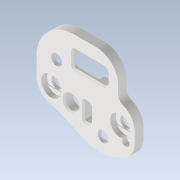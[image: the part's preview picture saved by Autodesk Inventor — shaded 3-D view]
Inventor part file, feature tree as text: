
AUTODESK INVENTOR PART (.ipt)
format: ipt  version: 2022.1 (Build 261234020, 234B)  size: 559,104 bytes
history: native  units: mm
features: reference x21, sketch x12, extrude x11, other x10, fillet x8, projected_geometry x7, delete_face x3, direct_edit x2, chamfer x2, move_body x2, hole x1
ambient origin geometry x8: Origin, YZ Plane, XZ Plane, XY Plane, X Axis, Y Axis, Z Axis, Center Point
bodies: Volumenkörper1 (feature_tree)
feature tree (79):
  extrude  "Extrusion1"  Depth=3.0mm
  delete_face  "Fläche löschen1"
  hole  "Bohrung1"  [1 undecoded]
  extrude  "Extrusion2"  Depth=1.0mm
  extrude  "Extrusion3"  Depth=0.8mm
  extrude  "Extrusion4"  Depth=1.0mm
  fillet  "Rundung1"  Radius=1.0mm
  fillet  "Rundung2"  Radius=1.0mm
  fillet  "Rundung3"  Radius=1.0mm
  delete_face  "Fläche löschen2"
  fillet  "Rundung4"  Radius=1.0mm
  fillet  "Rundung5"  Radius=1.0mm
  fillet  "Rundung6"  Radius=1.0mm
  fillet  "Rundung7"  Radius=1.0mm
  extrude  "Extrusion5"  Depth=1.0mm
  direct_edit  "Direktbearbeitung1"
  direct_edit  "Direktbearbeitung2"
  chamfer  "Fase2"  Distance=0.6mm
  extrude  "Extrusion6"  TaperAngle=0.0deg  [1 undecoded]
  extrude  "Extrusion7"  Depth=10.0mm
  extrude  "Extrusion8"  Depth=10.0mm
  chamfer  "Fase3"  Angle=45.0deg  [1 undecoded]
  fillet  "Rundung8"  Radius=4.0mm
  extrude  "Extrusion9"  Depth=10.0mm
  delete_face  "Fläche löschen3"
  extrude  "Extrusion10"  Depth=5.0mm
  extrude  "Extrusion11"  Depth=3.0mm
  sketch  "Skizze1"  dims[d0=2.0mm d1=0.0mm]
  reference  "Referenz1"
  reference  "Referenz2"
  reference  "Referenz3"
  reference  "Referenz4"
  reference  "Referenz5"
  reference  "Referenz6"
  reference  "Referenz7"
  reference  "Referenz8"
  reference  "Referenz9"
  reference  "Referenz10"
  reference  "Referenz11"
  reference  "Referenz12"
  sketch  "Skizze2"  dims[d2=3.0mm d3=6.0mm d4=4.0mm d5=2.0mm d6=90.0deg d7=8.0mm d8=20.594885mm d9=3.0mm]
  reference  "Referenz13"
  reference  "Referenz14"
  sketch  "Skizze3"  dims[d10=2.0mm d11=0.0mm d12=1.0mm]
  sketch  "Skizze4"  dims[d13=1.0mm d14=1.0mm]
  reference  "Referenz15"
  sketch  "Skizze5"  dims[d15=1.0mm d16=0.8mm]
  reference  "Referenz16"
  projected_geometry  "Projizierte Kontur1"
  sketch  "Skizze6"  dims[d17=1.0mm d18=1.0mm d19=1.0mm d20=1.0mm d21=1.0mm d22=1.0mm d23=1.0mm d24=1.0mm d25=1.0mm]
  sketch  "Skizze7"  dims[d26=1.0mm d27=1.0mm]
  sketch  "Skizze8"  dims[d28=1.0mm]
  projected_geometry  "Projizierte Kontur2"
  projected_geometry  "Projizierte Kontur3"
  sketch  "Skizze9"  dims[d29=1.0mm]
  reference  "Referenz17"
  reference  "Referenz18"
  sketch  "Skizze10"  dims[d30=1.0mm]
  reference  "Referenz19"
  reference  "Referenz20"
  reference  "Referenz21"
  sketch  "Skizze11"  dims[d31=1.0mm]
  projected_geometry  "Projizierte Kontur4"
  projected_geometry  "Projizierte Kontur5"
  sketch  "Skizze12"  dims[d32=1.0mm d33=0.6mm d34=0.0mm d35=0.0mm d36=4.0mm d37=4.0mm d38=45.0deg d39=4.0mm d40=4.0mm d41=5.0mm d42=3.0mm d43=3.0mm d44=0.0mm d45=0.0mm d46=2.4mm d47=5.0mm d48=2.0mm d49=6.0mm d50=10.0mm d51=5.0mm d52=10.0mm d53=10.0mm d57=5.5mm d58=5.5mm d59=5.5mm d60=5.5mm d61=1.6mm d62=0.0mm d63=0.0mm d64=0.0mm d65=0.4mm d66=1.0mm d67=0.0mm d68=0.0mm d69=0.4mm d70=2.0mm d71=45.0deg d72=5.6mm d73=5.6mm d74=1.6mm d75=0.0mm d76=0.2mm d77=0.0mm d78=1.4mm d79=0.0mm d80=0.4mm d81=2.0mm d82=45.0deg d83=2.0mm d84=1.0mm d85=1.0mm d86=1.0mm d87=1.0mm d88=0.8mm d89=0.0mm d90=0.0mm d91=10.0mm d92=0.0mm d93=10.0mm d94=0.0mm]
  projected_geometry  "Projizierte Kontur6"
  projected_geometry  "Projizierte Kontur7"
  other  "<userpath>\Desktop\RAMA_SBNG\Toolheads.iam"
  other  "Toolheads.iam"
  other  "LGX_Lite_Stealthburner_Normal:1"
  other  "Front_body_LGX_Lite_Stealthburner_rev02"
  other  "2PC-SB-PCB:1"
  other  "Bauteil52"
  other  "LGX-Lite Dummy"
  other  "<userpath>\Desktop\RAMA_SBNG\Baugruppe268.iam"
  other  "Baugruppe268.iam"
  move_body  "Verschieben1"
  move_body  "Verschieben2"
  other  "LGX-Lite Dummy:1"
note: 3 required parameter values undecoded (feature->parameter linkage not recoverable at this tier; creation-order binding heuristic only, values carry confidence <= 0.55)
